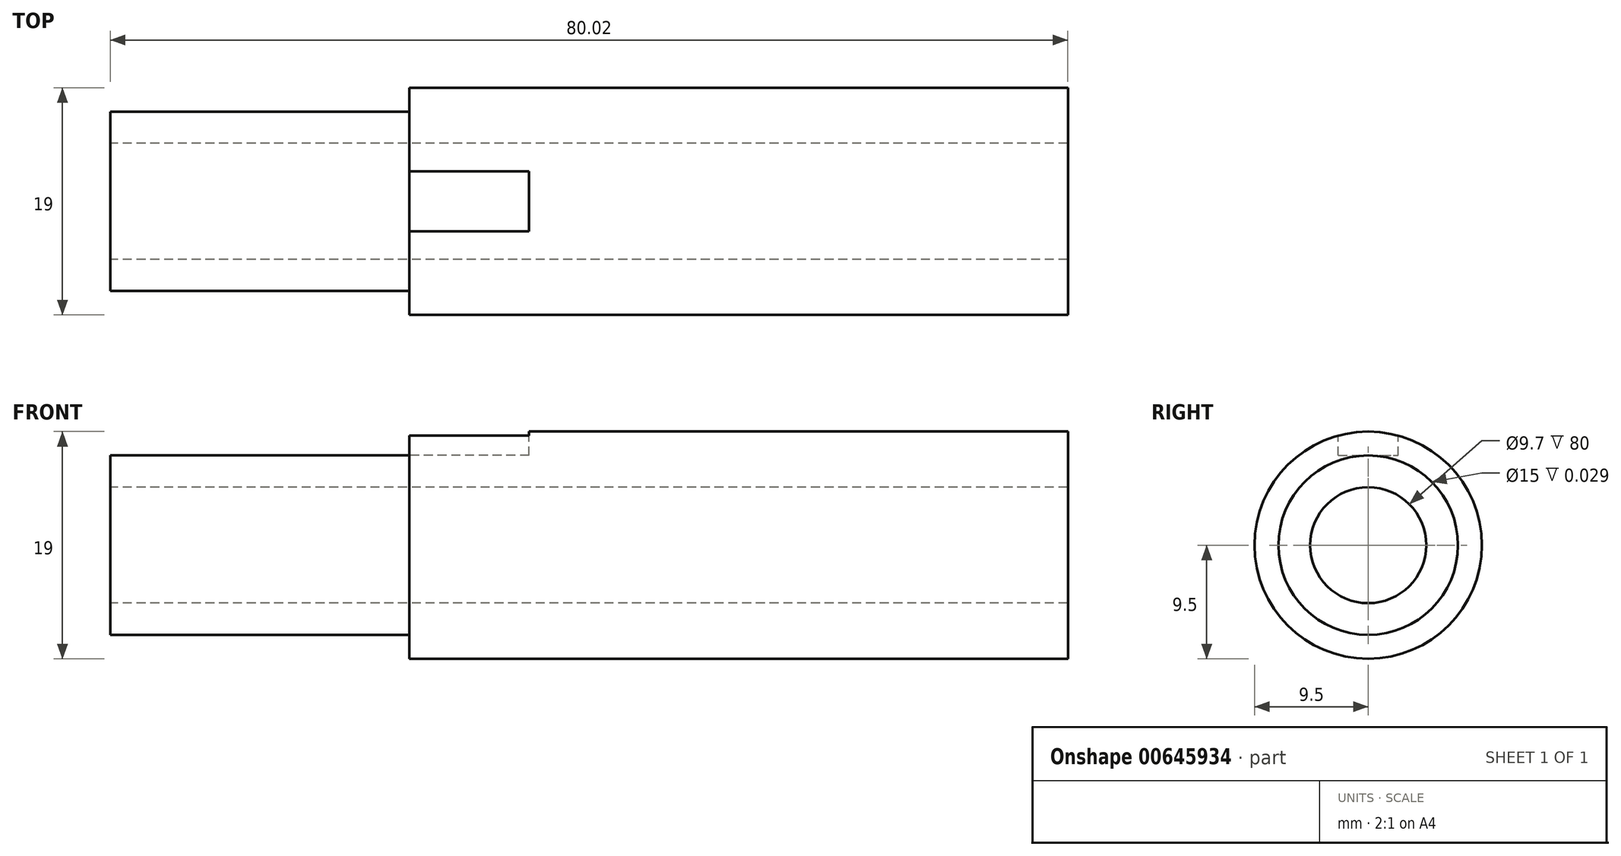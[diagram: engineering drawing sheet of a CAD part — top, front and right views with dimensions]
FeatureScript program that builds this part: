
annotation { "Feature Type Name" : "Feature", "Feature Type Description" : "" }
export const myFeature = defineFeature(function(context is Context, id is Id, definition is map)
    precondition{}
    {
        {
            var Q0;
            Q0=qCreatedBy(makeId("Front.planeOp"),FACE);
            var sketch = newSketch(context, id + "F0", { "sketchPlane" : qUnion([Q0])});
            skLineSegment(sketch, "E0", {"start": v(-45.68, 0) * mm, "end": v(46.24, 0) * mm, "construction": true});
            skLineSegment(sketch, "E1", {"start": v(-11.53, 4.85) * mm, "end": v(68.47, 4.85) * mm});
            skLineSegment(sketch, "E2", {"start": v(68.47, 4.85) * mm, "end": v(68.47, 7.5) * mm});
            skLineSegment(sketch, "E3", {"start": v(68.5, 7.5) * mm, "end": v(68.47, 7.5) * mm});
            skLineSegment(sketch, "E4", {"start": v(68.5, 7.5) * mm, "end": v(68.5, 9.5) * mm});
            skLineSegment(sketch, "E5", {"start": v(68.5, 9.5) * mm, "end": v(13.47, 9.5) * mm});
            skLineSegment(sketch, "E6", {"start": v(13.47, 9.5) * mm, "end": v(13.47, 7.5) * mm});
            skLineSegment(sketch, "E7", {"start": v(13.47, 7.5) * mm, "end": v(-11.53, 7.5) * mm});
            skLineSegment(sketch, "E8", {"start": v(-11.53, 7.5) * mm, "end": v(-11.53, 4.85) * mm});
            skSolve(sketch);
        }
        {
            var Q0;
            Q0=makeQuery(id+"F0.imprint","IMPRINT",FACE,{"disambiguationData":[TD([[makeQuery(id+"F0.imprint","IMPRINT",EDGE,{"derivedFrom":sQuery(id+"F0.wireOp",EDGE,"E1")}),1.0]])]});
            var Q1;
            Q1=sQuery(id+"F0.wireOp",EDGE,"E0");
            revolve(context, id + "F1", {"entities" : qUnion([Q0]), "axis" : qUnion([Q1]), "revolveType" : RevolveType.FULL});
        }
        {
            var Q0;
            Q0=makeQuery(id+"F1.opRevolve","SWEPT_FACE",FACE,{"disambiguationData":[OSD([sQuery(id+"F0.wireOp",EDGE,"E6")])]});
            var sketch = newSketch(context, id + "F2", { "sketchPlane" : qUnion([Q0])});
            skLineSegment(sketch, "E9.bottom", {"start": v(0, 7.5) * mm, "end": v(-2.5, 7.5) * mm});
            skLineSegment(sketch, "E9.top", {"start": v(0, 9.97) * mm, "end": v(-2.5, 9.97) * mm});
            skLineSegment(sketch, "E9.left", {"start": v(0, 7.5) * mm, "end": v(0, 9.97) * mm});
            skLineSegment(sketch, "E9.right", {"start": v(-2.5, 7.5) * mm, "end": v(-2.5, 9.97) * mm});
            skLineSegment(sketch, "E10.MirrorCS", {"start": v(0, 9.97) * mm, "end": v(2.5, 9.97) * mm});
            skLineSegment(sketch, "E11.MirrorCS", {"start": v(2.5, 7.5) * mm, "end": v(2.5, 9.97) * mm});
            skLineSegment(sketch, "E12.MirrorCS", {"start": v(0, 7.5) * mm, "end": v(2.5, 7.5) * mm});
            skSolve(sketch);
        }
        {
            var Q0;
            {var subQ0=sQuery(id+"F2.wireOp",EDGE,"E9.bottom");Q0=makeQuery(id+"F2.imprint","IMPRINT",FACE,{"disambiguationData":[TD([[makeQuery(id+"F2.imprint","IMPRINT",EDGE,{"derivedFrom":subQ0}),-1.0]])]});}
            var Q1;
            {var subQ0=sQuery(id+"F2.wireOp",EDGE,"E12.MirrorCS");Q1=makeQuery(id+"F2.imprint","IMPRINT",FACE,{"disambiguationData":[TD([[makeQuery(id+"F2.imprint","IMPRINT",EDGE,{"derivedFrom":subQ0}),1.0]])]});}
            extrude(context, id + "F3", {"entities" : qUnion([Q0, Q1]), "operationType" : NewBodyOperationType.REMOVE, "oppositeDirection" : true, "depth" : 10 * mm, "offsetDistance" : 25 * mm});
        }
    });
